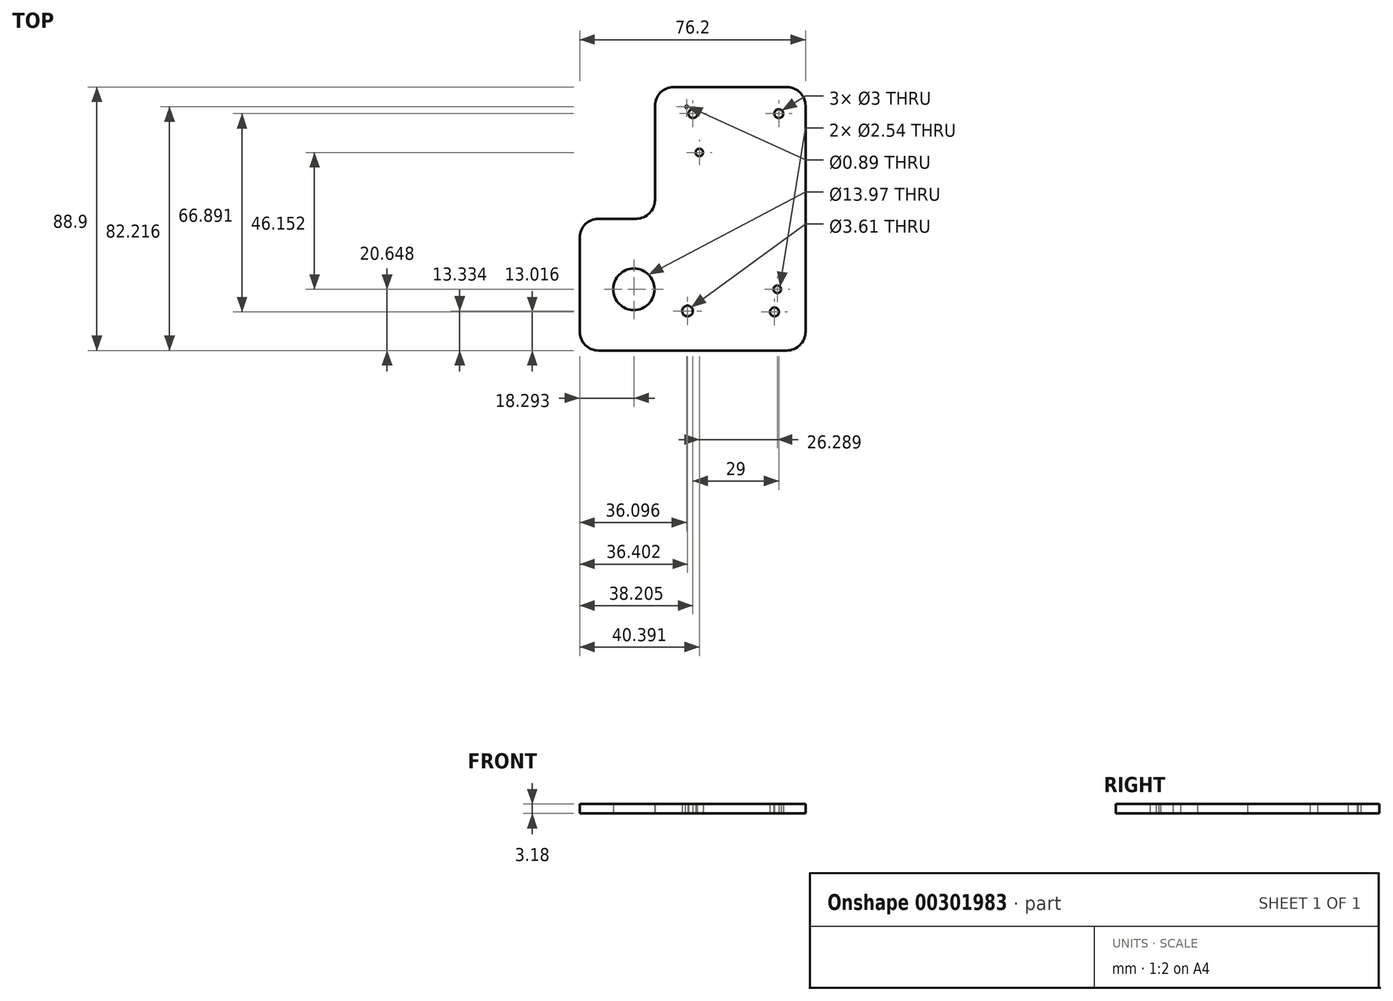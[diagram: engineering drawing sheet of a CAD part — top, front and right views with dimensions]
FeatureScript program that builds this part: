
annotation { "Feature Type Name" : "Feature", "Feature Type Description" : "" }
export const myFeature = defineFeature(function(context is Context, id is Id, definition is map)
    precondition{}
    {
        {
            var Q0;
            Q0=qCreatedBy(makeId("Top.planeOp"),FACE);
            var sketch = newSketch(context, id + "F0", { "sketchPlane" : qUnion([Q0])});
            skLineSegment(sketch, "E0", {"start": v(-25.25, -66.8) * mm, "end": v(38.25, -66.8) * mm});
            skLineSegment(sketch, "E1", {"start": v(44.6, -60.45) * mm, "end": v(44.6, 15.75) * mm});
            skLineSegment(sketch, "E2", {"start": v(38.25, 22.1) * mm, "end": v(0.15, 22.1) * mm});
            skLineSegment(sketch, "E3", {"start": v(-6.2, 15.75) * mm, "end": v(-6.2, -16) * mm});
            skLineSegment(sketch, "E4", {"start": v(-12.55, -22.35) * mm, "end": v(-25.25, -22.35) * mm});
            skLineSegment(sketch, "E5", {"start": v(-31.6, -28.7) * mm, "end": v(-31.6, -60.45) * mm});
            skPoint(sketch, "E6.visualSharp", {"position": v(-31.6, -66.8) * mm});
            skArc(sketch, "E6.filletArc", {"start": v(-31.6, -60.45) * mm, "mid": v(-29.74, -64.94) * mm, "end": v(-25.25, -66.8) * mm});
            skPoint(sketch, "E7.visualSharp", {"position": v(-31.6, -22.35) * mm});
            skArc(sketch, "E7.filletArc", {"start": v(-25.25, -22.35) * mm, "mid": v(-29.74, -24.21) * mm, "end": v(-31.6, -28.7) * mm});
            skPoint(sketch, "E8.newPointB", {"position": v(-6.2, -22.35) * mm});
            skArc(sketch, "E8.filletArc", {"start": v(-12.55, -22.35) * mm, "mid": v(-8.06, -20.5) * mm, "end": v(-6.2, -16) * mm});
            skPoint(sketch, "E9.visualSharp", {"position": v(-6.2, 22.1) * mm});
            skArc(sketch, "E9.filletArc", {"start": v(0.15, 22.1) * mm, "mid": v(-4.34, 20.24) * mm, "end": v(-6.2, 15.75) * mm});
            skPoint(sketch, "E10.visualSharp", {"position": v(44.6, 22.1) * mm});
            skArc(sketch, "E10.filletArc", {"start": v(44.6, 15.75) * mm, "mid": v(42.74, 20.24) * mm, "end": v(38.25, 22.1) * mm});
            skPoint(sketch, "E11.visualSharp", {"position": v(44.6, -66.8) * mm});
            skArc(sketch, "E11.filletArc", {"start": v(38.25, -66.8) * mm, "mid": v(42.74, -64.94) * mm, "end": v(44.6, -60.45) * mm});
            skCircle(sketch, "E12", {"center": v(-13.3, -46.15) * mm, "radius": 6.99 * mm});
            skCircle(sketch, "E13", {"center": v(8.8, 0) * mm, "radius": 1.27 * mm});
            skCircle(sketch, "E14", {"center": v(35.08, -46.15) * mm, "radius": 1.27 * mm});
            skCircle(sketch, "E15", {"center": v(4.5, 15.42) * mm, "radius": 0.44 * mm});
            skCircle(sketch, "E16", {"center": v(35.6, 13.1) * mm, "radius": 1.5 * mm});
            skCircle(sketch, "E17", {"center": v(6.6, 13.1) * mm, "radius": 1.5 * mm});
            skCircle(sketch, "E18", {"center": v(34.11, -53.78) * mm, "radius": 1.5 * mm});
            skCircle(sketch, "E19", {"center": v(4.8, -53.47) * mm, "radius": 1.8 * mm});
            skSolve(sketch);
        }
        {
            var Q0;
            Q0=makeQuery(id+"F0.imprint","IMPRINT",FACE,{"disambiguationData":[TD([[makeQuery(id+"F0.imprint","IMPRINT",EDGE,{"derivedFrom":sQuery(id+"F0.wireOp",EDGE,"E0")}),1.0]])]});
            extrude(context, id + "F1", {"entities" : qUnion([Q0]), "depth" : 3.17 * mm});
        }
    });
